# Revit family: Hekatron_Feststellanlagen_FSZ Kompakt si_DE_22.01
name_source: partatom
category: Brandmelder
revit_build: Autodesk Revit 2018 (Build: 20190510_1515(x64)
units: mm (PartAtom-declared; Revit-internal decimal feet)

## family parameters
Basisbauteil = Fläche
Beim Laden mit Abzugskörper schneiden = Nein
Bemaßung runder Anschluss = Durchmesser verwenden
Beschriftungsausrichtung beibehalten = Ja
Gemeinsam genutzt = Nein
OmniClass-Nummer = 23.85.30.21
OmniClass-Titel = Environmental Detection/Registration
Raumberechnungspunkt = Nein
Teiletyp = Normal

## types (1)
- FSZ Compact si
    Bauartgenehmigungen = Z-6.500-2394
    Beschreibung = Die FSZ Kompakt ist eine Feststellanlagenzentrale in kompakter Bauform und eignet sich für den Einsatz an Brand- und Rauchschutztüren. Durch die sehr kleine Bauform und ihr variables Design ist sie speziell für die Wand- oder Sturzmontage geeignet. Sie besteht aus Netzgerät, Alarmspeicher und Betriebszustandsanzeige. Zum Einsatz kommt sie in Feststellanlagen in den verschiedenen Anwendungen in Industrie- und Verwaltungsgebäuden.
    Betriebsspannung = 230 V AC
    Breite (mm) = 127.0
    Farbe = weiß, ähnlich RAL 9006
    Hersteller = Hekatron
    Höhe (mm) = 35.0
    Kabeleinführung = hinten, seitlich
    Link zu Ausschreibungstext = https://www.meinhplus.de
    Link zu ausschreiben.de = http://www.ausschreiben.de
    Material = PC
    Modell = FSZ Kompakt si
    Montageart = Wand- oder Sturzmontage
    Schutzart = IP 40
    Tiefe (mm) = 36.0
    Typenkommentare = Feststellanlagenzentrale Kompakt Standard si
    UB A&S Artikel Nummer = 31-5400007-04-01
    URL = https://www.hekatron-brandschutz.de
    VdS-Anerkennung = G 217098
    Version des BIM Objektes = 22.01
    Vorgabe-Ansicht = 1200 mm
    Zulässige Umgebungstemperatur = -20 °C bis +45 °C

## geometry (parser evidence)
native form markers: Extrusion x1, Sweep x2
no freeform markers — native parametric forms only
